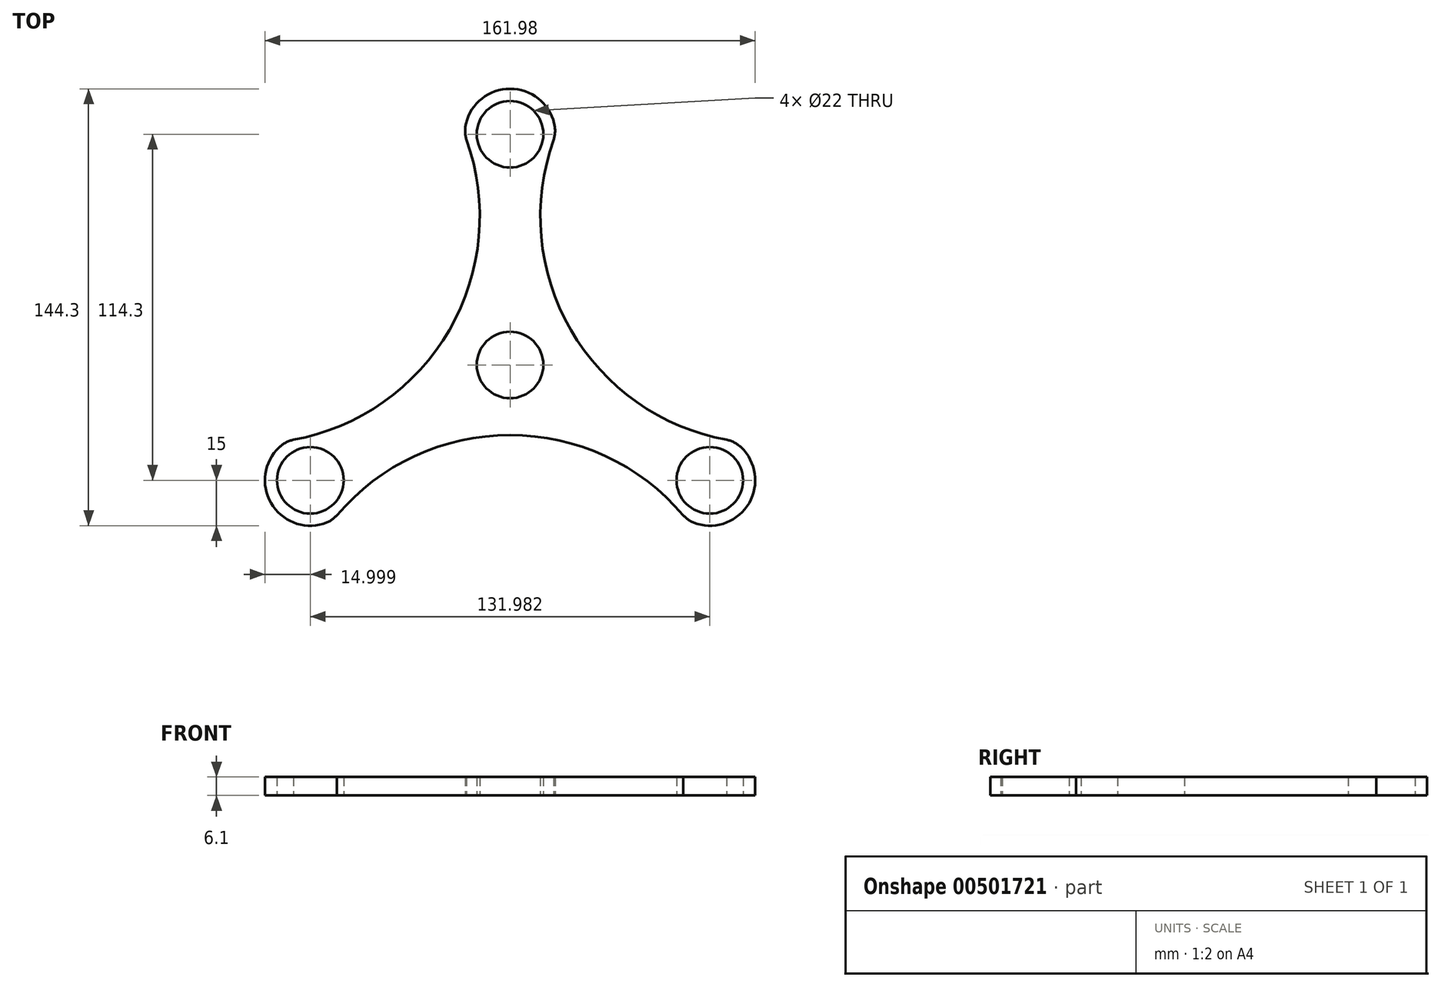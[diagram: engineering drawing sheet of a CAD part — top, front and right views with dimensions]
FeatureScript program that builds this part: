
annotation { "Feature Type Name" : "Feature", "Feature Type Description" : "" }
export const myFeature = defineFeature(function(context is Context, id is Id, definition is map)
    precondition{}
    {
        {
            var Q0;
            Q0=qCreatedBy(makeId("Top.planeOp"),FACE);
            var sketch = newSketch(context, id + "F0", { "sketchPlane" : qUnion([Q0])});
            skCircle(sketch, "E0", {"center": v(0, 76.2) * mm, "radius": 11 * mm});
            skCircle(sketch, "E1", {"center": v(0, 0) * mm, "radius": 11 * mm});
            skArc(sketch, "E2", {"start": v(14.58, 79.72) * mm, "mid": v(0, 91.2) * mm, "end": v(-14.58, 79.72) * mm});
            skPoint(sketch, "E3.visualSharp", {"position": v(-15, 76.2) * mm});
            skArc(sketch, "E3.filletArc", {"start": v(-14.58, 79.72) * mm, "mid": v(-14.85, 77.03) * mm, "end": v(-14.4, 74.37) * mm});
            skPoint(sketch, "E4.visualSharp", {"position": v(15, 76.2) * mm});
            skArc(sketch, "E4.filletArc", {"start": v(14.4, 74.37) * mm, "mid": v(14.85, 77.03) * mm, "end": v(14.58, 79.72) * mm});
            skArc(sketch, "E5", {"start": v(-71.6, -24.71) * mm, "mid": v(-20.05, 11.58) * mm, "end": v(-14.4, 74.37) * mm});
            skArc(sketch, "E6.1.0", {"start": v(57.2, -49.65) * mm, "mid": v(0, -23.16) * mm, "end": v(-57.2, -49.65) * mm});
            skCircle(sketch, "E6.1.2", {"center": v(-66, -38.1) * mm, "radius": 11 * mm});
            skPoint(sketch, "E6.1.3", {"position": v(-58.5, -51.1) * mm});
            skArc(sketch, "E6.1.4", {"start": v(-76.33, -27.23) * mm, "mid": v(-78.98, -45.6) * mm, "end": v(-61.74, -52.49) * mm});
            skPoint(sketch, "E6.1.5", {"position": v(-73.5, -25.1) * mm});
            skArc(sketch, "E6.1.6", {"start": v(-71.6, -24.71) * mm, "mid": v(-74.14, -25.65) * mm, "end": v(-76.33, -27.23) * mm});
            skArc(sketch, "E6.1.8", {"start": v(-61.74, -52.49) * mm, "mid": v(-59.28, -51.38) * mm, "end": v(-57.2, -49.65) * mm});
            skArc(sketch, "E6.2.0", {"start": v(14.4, 74.37) * mm, "mid": v(20.05, 11.58) * mm, "end": v(71.6, -24.71) * mm});
            skCircle(sketch, "E6.2.2", {"center": v(66, -38.1) * mm, "radius": 11 * mm});
            skPoint(sketch, "E6.2.3", {"position": v(73.5, -25.1) * mm});
            skArc(sketch, "E6.2.4", {"start": v(61.74, -52.49) * mm, "mid": v(78.98, -45.6) * mm, "end": v(76.33, -27.23) * mm});
            skPoint(sketch, "E6.2.5", {"position": v(58.5, -51.1) * mm});
            skArc(sketch, "E6.2.6", {"start": v(57.2, -49.65) * mm, "mid": v(59.28, -51.38) * mm, "end": v(61.74, -52.49) * mm});
            skArc(sketch, "E6.2.8", {"start": v(76.33, -27.23) * mm, "mid": v(74.14, -25.65) * mm, "end": v(71.6, -24.71) * mm});
            skSolve(sketch);
        }
        {
            var Q0;
            Q0=makeQuery(id+"F0.imprint","IMPRINT",FACE,{"disambiguationData":[TD([[makeQuery(id+"F0.imprint","IMPRINT",EDGE,{"derivedFrom":sQuery(id+"F0.wireOp",EDGE,"E0")}),-1.0]])]});
            extrude(context, id + "F1", {"entities" : qUnion([Q0]), "depth" : 6.1 * mm});
        }
    });
